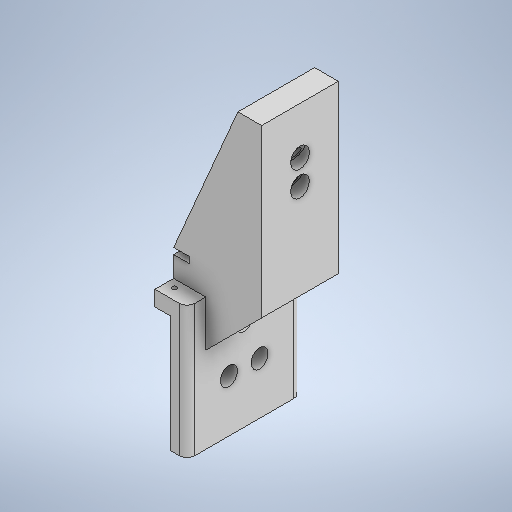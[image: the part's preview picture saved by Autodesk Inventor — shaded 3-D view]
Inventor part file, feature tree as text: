
AUTODESK INVENTOR PART (.ipt)
format: ipt  version: 2025.2 (Build 292293000, 293)  size: 442,880 bytes
history: native  units: in
note: dims shown in document units (in); Inventor stores cm internally (conversion verified against a paired STEP export)
features: extrude x18, sketch x14, plane x6, chamfer x2, fillet x1, projected_geometry x1
ambient origin geometry x8: Origin, YZ Plane, XZ Plane, XY Plane, X Axis, Y Axis, Z Axis, Center Point
bodies: Solid1 (feature_tree)
feature tree (42):
  sketch  "Sketch1"  dims[d0=0.4331in d1=2.9331in]
  extrude  "Extrusion1"  Depth=2.9331in
  extrude  "Extrusion2"  Depth=0.2854in
  extrude  "Extrusion3"  Depth=0.3937in TaperAngle=0.0deg
  plane  "Work Plane1"
  plane  "Work Plane3"
  sketch  "Sketch4"  dims[d9=0.4213in d10=2.9921in d11=0.0in]
  extrude  "Extrusion4"  Depth=2.9921in TaperAngle=0.0deg
  extrude  "Extrusion11"  Depth=0.1575in
  extrude  "Extrusion6"  Depth=0.1575in
  extrude  "Extrusion7"  Depth=0.3937in
  extrude  "Extrusion8"  Depth=2.1457in
  chamfer  "Chamfer1"  [1 undecoded]
  chamfer  "Chamfer2"  Distance=4.9213in
  extrude  "Extrusion12"  Depth=0.0787in
  plane  "Work Plane4"
  plane  "Work Plane5"
  plane  "Work Plane6"
  extrude  "Extrusion15"  Depth=0.1969in
  fillet  "Fillet1"  Radius=1.0207in
  extrude  "Extrusion16"  Depth=1.9685in TaperAngle=0.0deg
  extrude  "Extrusion18"  TaperAngle=0.0deg  [1 undecoded]
  extrude  "Extrusion19"  Depth=0.3937in
  extrude  "Extrusion20"  Depth=0.1575in
  extrude  "Extrusion22"  Depth=0.3937in TaperAngle=0.0deg
  plane  "Work Plane8"
  sketch  "Sketch19"  dims[d62=-1.378in d68=0.0in]
  extrude  "Extrusion23"  Depth=0.1969in
  extrude  "Extrusion24"  Depth=0.2362in
  extrude  "Extrusion25"  Depth=0.2362in
  sketch  "Sketch2"  dims[d2=0.1181in d3=0.2854in]
  sketch  "Sketch3"  dims[d5=0.3937in d6=0.0in d7=0.3937in d8=0.0in]
  sketch  "Sketch5"  dims[d12=1.0668in d13=0.1575in]
  sketch  "Sketch8"  dims[d14=0.4331in d15=0.1575in d16=0.4331in]
  sketch  "Sketch11"  dims[d19=0.3937in d20=0.9331in]
  sketch  "Sketch12"  dims[d21=0.5906in d22=0.0in d23=2.1457in d26=0.0in d27=0.0in]
  sketch  "Sketch14"  dims[d28=1.9685in d29=4.9213in d30=0.0in]
  sketch  "Sketch15"  dims[d31=1.5748in d32=0.0in d33=1.5748in d34=0.0787in d35=0.1598in]
  projected_geometry  "Projected Loop1"
  sketch  "Sketch16"  dims[d51=1.1811in d52=1.1811in d53=0.7782in d56=0.1969in d57=1.0207in d58=0.0in]
  sketch  "Sketch18"  dims[d59=1.9685in d60=0.8937in d61=0.0in]
  sketch  "Sketch20"  dims[d69=90.0deg d76=0.3937in d77=0.1575in d78=2.7756in d79=0.0in d80=0.1969in d81=0.2362in d82=0.2362in d83=0.3937in d84=0.3543in d85=0.0in d88=0.2756in d89=0.0in d91=135.0deg d92=1.9685in d93=0.0in d94=0.3543in d95=0.0in d99=0.4724in d100=0.748in d103=0.2756in d104=0.2756in d105=0.5906in d106=0.3937in d107=0.0in d108=-0.9843in d109=0.4724in d110=0.4724in d111=0.5906in d112=0.0in d113=0.7874in d114=0.0in d115=0.0in d116=0.0in d117=0.0197in d118=0.0344in d119=0.0197in d120=0.0344in]
note: 2 required parameter values undecoded (feature->parameter linkage not recoverable at this tier; creation-order binding heuristic only, values carry confidence <= 0.55)
